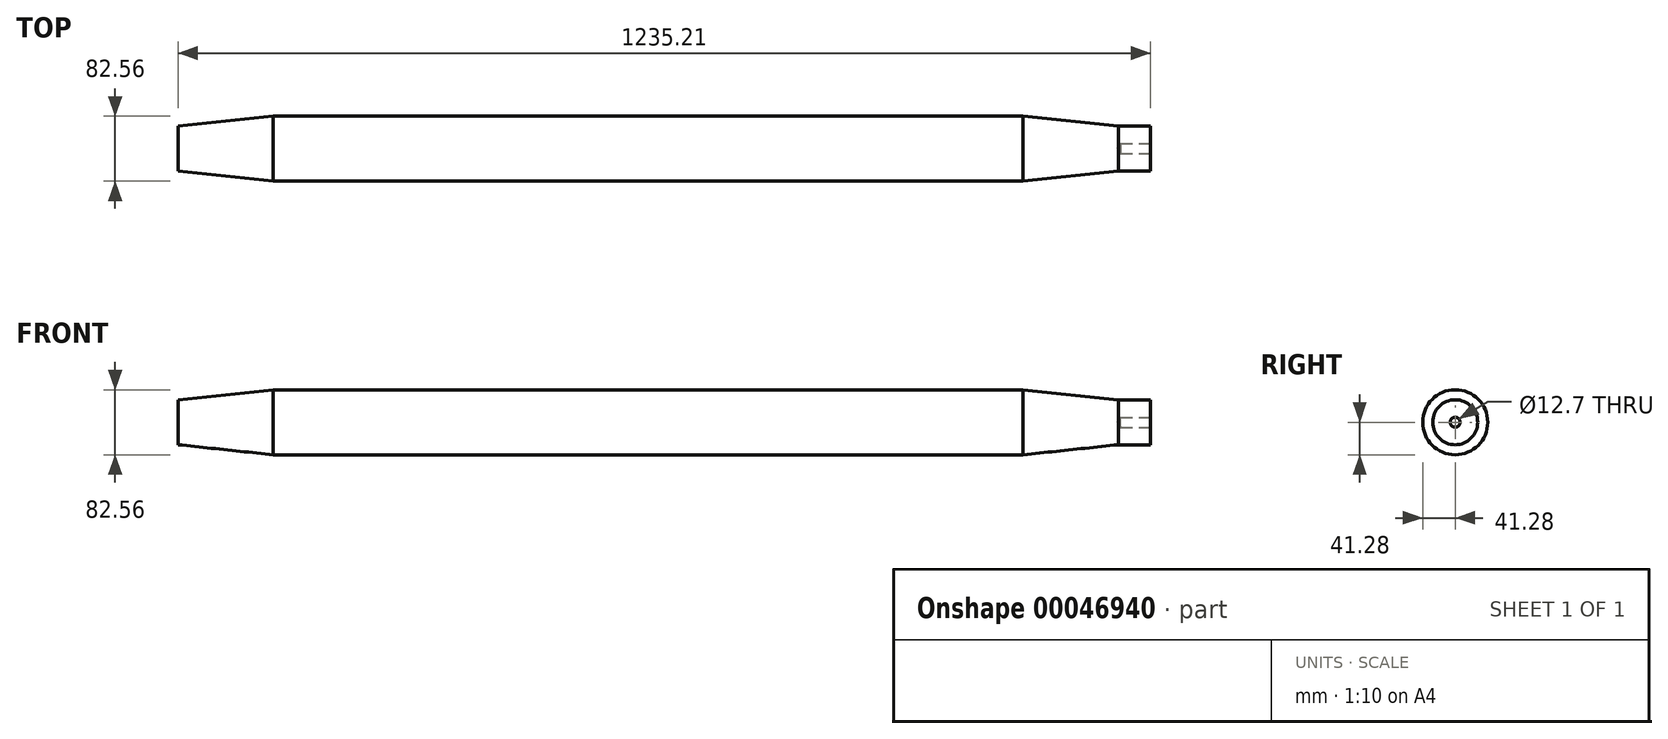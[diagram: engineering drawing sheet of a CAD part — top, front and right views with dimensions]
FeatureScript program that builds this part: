
annotation { "Feature Type Name" : "Feature", "Feature Type Description" : "" }
export const myFeature = defineFeature(function(context is Context, id is Id, definition is map)
    precondition{}
    {
        {
            var Q0;
            Q0=qCreatedBy(makeId("Right.planeOp"),FACE);
            var sketch = newSketch(context, id + "F0", { "sketchPlane" : qUnion([Q0])});
            skCircle(sketch, "E0", {"center": v(0, 0) * mm, "radius": 41.28 * mm});
            skSolve(sketch);
        }
        {
            var Q0;
            Q0 = qSketchRegion(id + "F0", true);
            extrude(context, id + "F1", {"entities" : qUnion([Q0]), "endBound" : BoundingType.SYMMETRIC, "depth" : 952.5 * mm});
        }
        {
            var Q0;
            Q0=qCreatedBy(makeId("Right.planeOp"),FACE);
            cPlane(context, id + "F2", {"entities" : qUnion([Q0]), "cplaneType" : CPlaneType.OFFSET, "offset" : 638.17 * mm, "width" : 152.4 * mm, "height" : 152.4 * mm});
        }
        {
            var Q0;
            Q0=qCreatedBy(id+"F2.planeOp",FACE);
            var sketch = newSketch(context, id + "F3", { "sketchPlane" : qUnion([Q0])});
            skCircle(sketch, "E1", {"center": v(0, 0) * mm, "radius": 28.57 * mm});
            skSolve(sketch);
        }
        {
            var Q0;
            Q0 = qSketchRegion(id + "F3", true);
            extrude(context, id + "F4", {"entities" : qUnion([Q0]), "oppositeDirection" : true, "depth" : 41.15 * mm});
        }
        {
            var Q0;
            Q0=makeQuery(id+"F1.opExtrude","CAP_FACE",FACE,{"disambiguationData":[OSD([sQuery(id+"F0.wireOp",EDGE,"E0")])],"isStart":false});
            var Q1;
            Q1=makeQuery(id+"F4.opExtrude","CAP_FACE",FACE,{"disambiguationData":[OSD([sQuery(id+"F3.wireOp",EDGE,"E1")])],"isStart":false});
            loft(context, id + "F5", {"sheetProfilesArray" : [{ "sheetProfileEntities" : qUnion([Q0]) }, { "sheetProfileEntities" : qUnion([Q1]) }]});
        }
        {
            var Q0;
            Q0=makeQuery(id+"F5.opLoft","SWEPT_BODY",BODY,{"disambiguationData":[OSD([sQuery(id+"F0.wireOp",EDGE,"E0"),sQuery(id+"F3.wireOp",EDGE,"E1")])]});
            var Q1;
            Q1=qCreatedBy(makeId("Right.planeOp"),FACE);
            mirror(context, id + "F6", {"operationType" : NewBodyOperationType.ADD, "entities" : qUnion([Q0]), "mirrorPlane" : qUnion([Q1])});
        }
        {
            var Q0;
            Q0=qCreatedBy(id+"F2.planeOp",FACE);
            var sketch = newSketch(context, id + "F7", { "sketchPlane" : qUnion([Q0])});
            skPoint(sketch, "E2", {"position": v(0, 0) * mm});
            skSolve(sketch);
        }
        {
            var Q0;
            Q0=makeQuery(id+"F6.opPattern","COPY",FACE,{"derivedFrom":makeQuery(id+"F4.opExtrude","CAP_FACE",FACE,{"disambiguationData":[OSD([sQuery(id+"F3.wireOp",EDGE,"E1")])],"isStart":true}),"instanceName":"1"});
            var sketch = newSketch(context, id + "F8", { "sketchPlane" : qUnion([Q0])});
            skPoint(sketch, "E3", {"position": v(0, 0) * mm});
            skSolve(sketch);
        }
        {
            var Q0;
            Q0=sQuery(id+"F8.wireOp",VERTEX,"E3");
            var Q1;
            Q1=sQuery(id+"F7.wireOp",VERTEX,"E2");
            var Q2;
            Q2=makeQuery(id+"F1.opExtrude","SWEPT_BODY",BODY,{"disambiguationData":[OSD([sQuery(id+"F0.wireOp",EDGE,"E0")])]});
            hole(context, id + "F9", {"style" : HoleStyle.SIMPLE, "holeDiameter" : 12.7 * mm, "endStyle" : HoleEndStyle.BLIND, "holeDepth" : 38.1 * mm, "locations" : qUnion([Q0, Q1]), "scope" : qUnion([Q2])});
        }
    });
